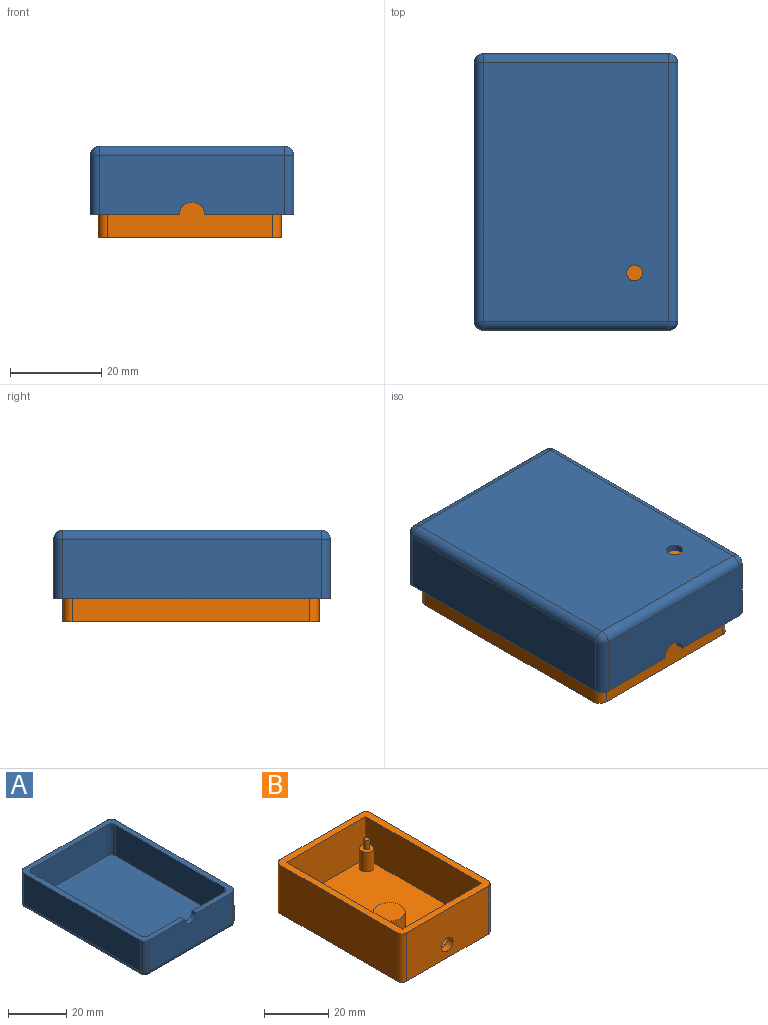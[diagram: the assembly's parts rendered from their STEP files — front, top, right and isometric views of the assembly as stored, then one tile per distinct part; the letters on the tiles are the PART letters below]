
ASSEMBLY  parts=2 mates=1
PART A: 31 faces, bbox 44.5x60.5x15 mm
  f0: plane 36.5x13mm, normal (0,1,0), area 462.6mm2, adj f9,f10,f13,f14,f28
  f1: plane 56.5x13mm, normal (1,0,0), area 734.5mm2, adj f9,f20,f24,f26
  f2: plane 40.5x13mm, normal (0,1,0), area 526.5mm2, adj f9,f17,f23,f26
  f3: plane 56.5x13mm, normal (-1,0,0), area 734.5mm2, adj f9,f15,f17,f18
  f4: plane 40.5x13mm, normal (0,-1,0), area 514.6mm2, adj f9,f15,f19,f20,f28
  f5: plane 56.5x40.5mm, normal (0,0,-1), area 2278.6mm2, adj f18,f19,f23,f24,f27
  f6: plane 52.5x13mm, normal (1,0,0), area 682.5mm2, adj f9,f10,f11,f14
  f7: plane 36.5x13mm, normal (0,-1,0), area 474.5mm2, adj f9,f10,f11,f12
  f8: plane 52.5x13mm, normal (-1,0,0), area 682.5mm2, adj f9,f10,f12,f13
  f9: plane 60.5x44.5mm, normal (0,0,1), area 393mm2, adj f0,f1,f2,f3,f4,f6,f7,f8
  f10: plane 56.5x40.5mm, normal (0,0,1), area 2256.5mm2, adj f0,f6,f7,f8,f11,f12,f13,f14
  f11: cylinder r=2mm len=13mm, axis (0,0,-1), area 40.8mm2, adj f6,f7,f9,f10
  f12: cylinder r=2mm len=13mm, axis (0,0,1), area 40.8mm2, adj f7,f8,f9,f10
  f13: cylinder r=2mm len=13mm, axis (0,0,-1), area 40.8mm2, adj f0,f8,f9,f10
  f14: cylinder r=2mm len=13mm, axis (0,0,1), area 40.8mm2, adj f0,f6,f9,f10
  f15: cylinder r=2mm len=13mm, axis (0,0,1), area 40.8mm2, adj f3,f4,f9,f16
  f16: sphere r=2mm, area 6.3mm2, adj f15,f18,f19
  f17: cylinder r=2mm len=13mm, axis (0,0,-1), area 40.8mm2, adj f2,f3,f9,f21
  f18: cylinder r=2mm len=56.5mm, axis (0,1,0), area 177.5mm2, adj f3,f5,f16,f21
  f19: cylinder r=2mm len=40.5mm, axis (-1,0,0), area 127.2mm2, adj f4,f5,f16,f22
  f20: cylinder r=2mm len=13mm, axis (0,0,-1), area 40.8mm2, adj f1,f4,f9,f22
  f21: sphere r=2mm, area 6.3mm2, adj f17,f18,f23
  f22: sphere r=2mm, area 6.3mm2, adj f19,f20,f24
  f23: cylinder r=2mm len=40.5mm, axis (1,0,0), area 127.2mm2, adj f2,f5,f21,f25
  f24: cylinder r=2mm len=56.5mm, axis (0,-1,0), area 177.5mm2, adj f1,f5,f22,f25
  f25: sphere r=2mm, area 6.3mm2, adj f23,f24,f26
  f26: cylinder r=2mm len=13mm, axis (0,0,1), area 40.8mm2, adj f1,f2,f9,f25
  f27: cylinder r=1.75mm len=3.5mm, axis (0,0,1), area 38.5mm2, adj f5,f30
  f28: cylinder r=2.75mm len=5.5mm, axis (0,-1,0), area 17.3mm2, adj f0,f4,f9
  f29: cylinder r=3mm len=6mm, axis (0,0,-1), area 28.3mm2, adj f10,f30
  f30: plane 6x6mm, normal (0,0,1), area 18.7mm2, adj f27,f29
PART B: 26 faces, bbox 40x56x18.5 mm
  f0: plane 52x18.5mm, normal (-1,0,0), area 962mm2, adj f8,f10,f19,f22
  f1: plane 36x18.5mm, normal (0,-1,0), area 645.6mm2, adj f8,f10,f19,f20,f25
  f2: plane 52x18.5mm, normal (1,0,0), area 962mm2, adj f8,f10,f20,f21
  f3: plane 51x16mm, normal (-1,0,0), area 816mm2, adj f4,f6,f8,f9
  f4: plane 35x16mm, normal (0,1,0), area 539.6mm2, adj f3,f5,f8,f9,f25
  f5: plane 51x16mm, normal (1,0,0), area 816mm2, adj f4,f6,f8,f9
  f6: plane 35x16mm, normal (0,-1,0), area 560mm2, adj f3,f5,f8,f9
  f7: plane 36x18.5mm, normal (0,1,0), area 666mm2, adj f8,f10,f21,f22
  f8: plane 56x40mm, normal (0,0,1), area 451.6mm2, adj f0,f1,f2,f3,f4,f5,f6,f7
  f9: plane 51x35mm, normal (0,0,1), area 1674.7mm2, adj f3,f4,f5,f6,f11,f13,f23
  f10: plane 56x40mm, normal (0,0,-1), area 2236.6mm2, adj f0,f1,f2,f7,f19,f20,f21,f22
  f11: cylinder r=2.25mm len=7.5mm, axis (0,0,-1), area 106mm2, adj f9,f12
  f12: plane 4.5x4.5mm, normal (0,0,1), area 13.4mm2, adj f11,f15
  f13: cylinder r=2.25mm len=7.5mm, axis (0,0,-1), area 106mm2, adj f9,f14
  f14: plane 4.5x4.5mm, normal (0,0,1), area 13.4mm2, adj f13,f17
  f15: cylinder r=0.9mm len=3.5mm, axis (0,0,-1), area 19.8mm2, adj f12,f16
  f16: plane 1.8x1.8mm, normal (0,0,1), area 2.5mm2, adj f15
  f17: cylinder r=0.9mm len=3.5mm, axis (0,0,-1), area 19.8mm2, adj f14,f18
  f18: plane 1.8x1.8mm, normal (0,0,1), area 2.5mm2, adj f17
  f19: cylinder r=2mm len=18.5mm, axis (0,0,-1), area 58.1mm2, adj f0,f1,f8,f10
  f20: cylinder r=2mm len=18.5mm, axis (0,0,1), area 58.1mm2, adj f1,f2,f8,f10
  f21: cylinder r=2mm len=18.5mm, axis (0,0,-1), area 58.1mm2, adj f2,f7,f8,f10
  f22: cylinder r=2mm len=18.5mm, axis (0,0,1), area 58.1mm2, adj f0,f7,f8,f10
  f23: cylinder r=5mm len=11.8mm, axis (0,0,-1), area 370.7mm2, adj f9,f24
  f24: plane 10x10mm, normal (0,0,1), area 78.5mm2, adj f23
  f25: cylinder r=2.55mm len=5.1mm, axis (0,-1,0), area 40.1mm2, adj f1,f4
PLACE A rot(axis=(0,1,0),180deg) t=(120.32,-0.51,5.12)mm
PLACE B rot(axis=(1,0,0),180deg) t=(51.42,-2.35,3.12)mm
MATE slider B.f9 <-> A.f5  axis (0,0,-1) through (51.87,-2.5,3.12)mm
